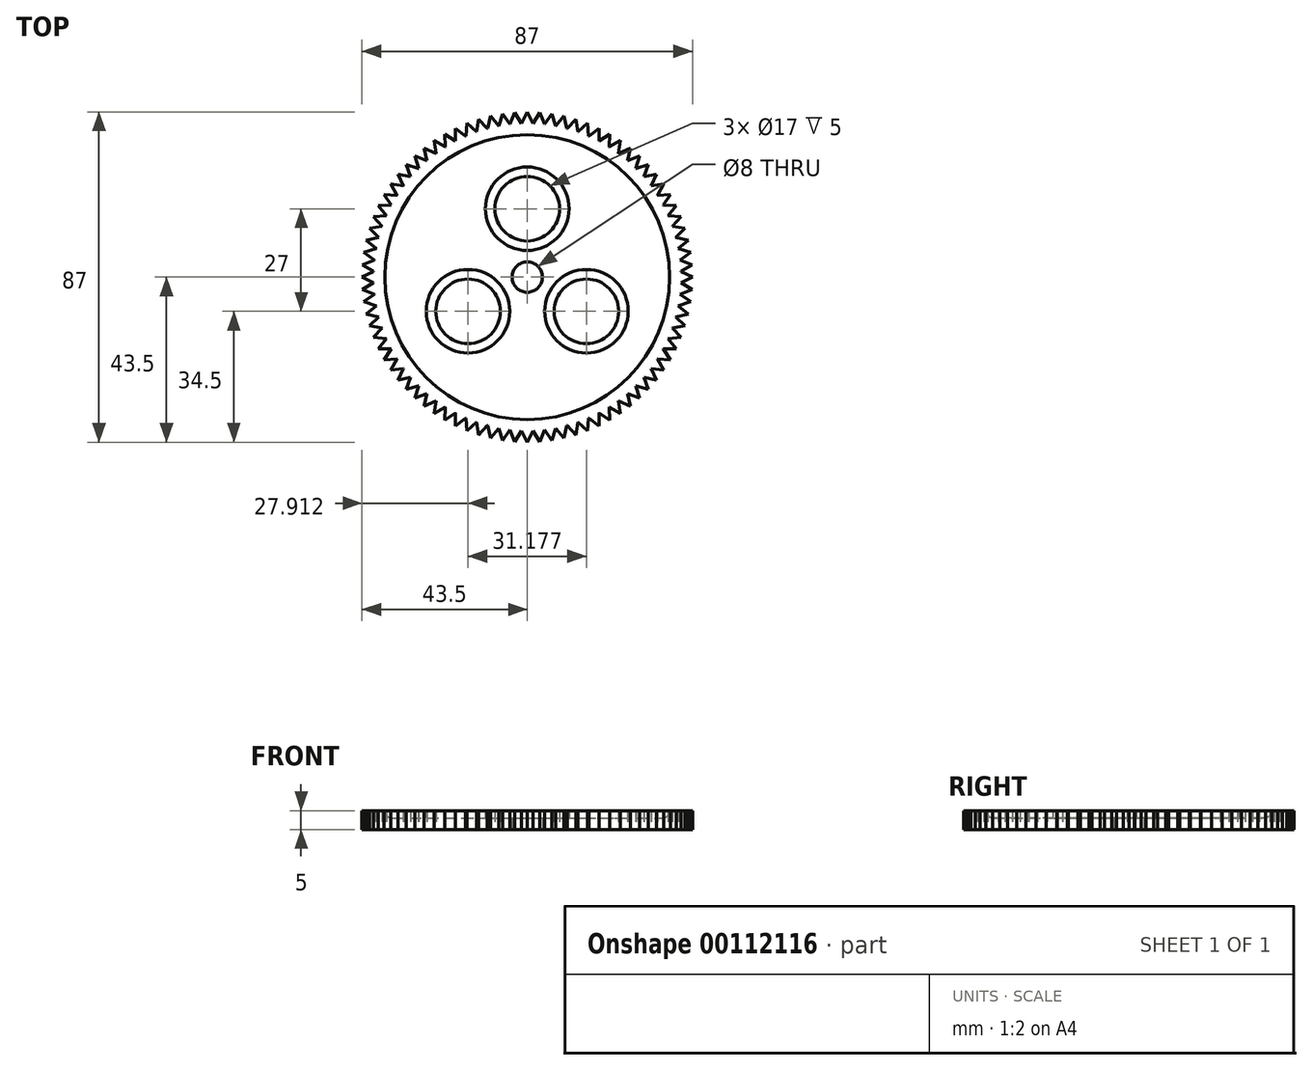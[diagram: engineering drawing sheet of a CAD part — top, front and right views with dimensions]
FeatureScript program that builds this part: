
annotation { "Feature Type Name" : "Feature", "Feature Type Description" : "" }
export const myFeature = defineFeature(function(context is Context, id is Id, definition is map)
    precondition{}
    {
        {
            var Q0;
            Q0=qCreatedBy(makeId("Front.planeOp"),FACE);
            var sketch = newSketch(context, id + "F0", { "sketchPlane" : qUnion([Q0])});
            skLineSegment(sketch, "E0", {"start": v(0, 0) * mm, "end": v(40.5, 0) * mm});
            skLineSegment(sketch, "E1", {"start": v(0, -1.2) * mm, "end": v(0, 3) * mm});
            skLineSegment(sketch, "E2", {"start": v(0, 3) * mm, "end": v(35.5, 3) * mm});
            skLineSegment(sketch, "E3", {"start": v(37.5, 5) * mm, "end": v(37.5, 5) * mm});
            skLineSegment(sketch, "E4", {"start": v(37.5, 5) * mm, "end": v(40.5, 5) * mm});
            skLineSegment(sketch, "E5", {"start": v(40.5, 5) * mm, "end": v(40.5, 0) * mm});
            skPoint(sketch, "E6.visualSharp", {"position": v(37.5, 3) * mm});
            skArc(sketch, "E6.filletArc", {"start": v(35.5, 3) * mm, "mid": v(36.91, 3.59) * mm, "end": v(37.5, 5) * mm});
            skLineSegment(sketch, "E7", {"start": v(4, 3) * mm, "end": v(4, 0) * mm});
            skSolve(sketch);
        }
        {
            var Q0;
            Q0=makeQuery(id+"F0.imprint","IMPRINT",FACE,{"disambiguationData":[TD([[makeQuery(id+"F0.imprint","IMPRINT",EDGE,{"derivedFrom":sQuery(id+"F0.wireOp",EDGE,"E4")}),-1.0]])]});
            var Q1;
            Q1=sQuery(id+"F0.wireOp",EDGE,"E1");
            revolve(context, id + "F1", {"entities" : qUnion([Q0]), "axis" : qUnion([Q1]), "revolveType" : RevolveType.FULL});
        }
        {
            var Q0;
            Q0=qCreatedBy(makeId("Top.planeOp"),FACE);
            var sketch = newSketch(context, id + "F2", { "sketchPlane" : qUnion([Q0])});
            skCircle(sketch, "E8.0.0", {"center": v(0, 0) * mm, "radius": 40.5 * mm});
            skLineSegment(sketch, "E9", {"start": v(0, 40.5) * mm, "end": v(0, 43.5) * mm});
            skLineSegment(sketch, "E10", {"start": v(0, 43.5) * mm, "end": v(-1.5, 40.47) * mm});
            skLineSegment(sketch, "E11", {"start": v(0, 43.5) * mm, "end": v(1.5, 40.47) * mm});
            skLineSegment(sketch, "E12.1.0", {"start": v(-3.25, 43.38) * mm, "end": v(-4.52, 40.25) * mm});
            skLineSegment(sketch, "E12.1.1", {"start": v(-3.25, 43.38) * mm, "end": v(-1.53, 40.47) * mm});
            skLineSegment(sketch, "E12.2.0", {"start": v(-6.48, 43.01) * mm, "end": v(-7.52, 39.8) * mm});
            skLineSegment(sketch, "E12.2.1", {"start": v(-6.48, 43.01) * mm, "end": v(-4.55, 40.24) * mm});
            skLineSegment(sketch, "E12.3.0", {"start": v(-9.68, 42.4) * mm, "end": v(-10.47, 39.12) * mm});
            skLineSegment(sketch, "E12.3.1", {"start": v(-9.68, 42.4) * mm, "end": v(-7.54, 39.8) * mm});
            skLineSegment(sketch, "E12.4.0", {"start": v(-12.82, 41.57) * mm, "end": v(-13.36, 38.23) * mm});
            skLineSegment(sketch, "E12.4.1", {"start": v(-12.82, 41.57) * mm, "end": v(-10.5, 39.12) * mm});
            skLineSegment(sketch, "E12.5.0", {"start": v(-15.9, 40.5) * mm, "end": v(-16.18, 37.13) * mm});
            skLineSegment(sketch, "E12.5.1", {"start": v(-15.9, 40.5) * mm, "end": v(-13.39, 38.22) * mm});
            skLineSegment(sketch, "E12.6.0", {"start": v(-18.87, 39.2) * mm, "end": v(-18.91, 35.81) * mm});
            skLineSegment(sketch, "E12.6.1", {"start": v(-18.87, 39.2) * mm, "end": v(-16.2, 37.12) * mm});
            skLineSegment(sketch, "E12.7.0", {"start": v(-21.75, 37.67) * mm, "end": v(-21.54, 34.3) * mm});
            skLineSegment(sketch, "E12.7.1", {"start": v(-21.75, 37.67) * mm, "end": v(-18.94, 35.8) * mm});
            skLineSegment(sketch, "E12.8.0", {"start": v(-24.5, 35.94) * mm, "end": v(-24.04, 32.6) * mm});
            skLineSegment(sketch, "E12.8.1", {"start": v(-24.5, 35.94) * mm, "end": v(-21.56, 34.28) * mm});
            skLineSegment(sketch, "E12.9.0", {"start": v(-27.12, 34) * mm, "end": v(-26.4, 30.7) * mm});
            skLineSegment(sketch, "E12.9.1", {"start": v(-27.12, 34) * mm, "end": v(-24.06, 32.58) * mm});
            skLineSegment(sketch, "E12.10.0", {"start": v(-29.59, 31.89) * mm, "end": v(-28.63, 28.65) * mm});
            skLineSegment(sketch, "E12.10.1", {"start": v(-29.59, 31.89) * mm, "end": v(-26.43, 30.69) * mm});
            skLineSegment(sketch, "E12.11.0", {"start": v(-31.89, 29.59) * mm, "end": v(-30.69, 26.43) * mm});
            skLineSegment(sketch, "E12.11.1", {"start": v(-31.89, 29.59) * mm, "end": v(-28.65, 28.63) * mm});
            skLineSegment(sketch, "E12.12.0", {"start": v(-34, 27.12) * mm, "end": v(-32.58, 24.06) * mm});
            skLineSegment(sketch, "E12.12.1", {"start": v(-34, 27.12) * mm, "end": v(-30.7, 26.4) * mm});
            skLineSegment(sketch, "E12.13.0", {"start": v(-35.94, 24.5) * mm, "end": v(-34.28, 21.56) * mm});
            skLineSegment(sketch, "E12.13.1", {"start": v(-35.94, 24.5) * mm, "end": v(-32.6, 24.04) * mm});
            skLineSegment(sketch, "E12.14.0", {"start": v(-37.67, 21.75) * mm, "end": v(-35.8, 18.94) * mm});
            skLineSegment(sketch, "E12.14.1", {"start": v(-37.67, 21.75) * mm, "end": v(-34.3, 21.54) * mm});
            skLineSegment(sketch, "E12.15.0", {"start": v(-39.2, 18.87) * mm, "end": v(-37.12, 16.2) * mm});
            skLineSegment(sketch, "E12.15.1", {"start": v(-39.2, 18.87) * mm, "end": v(-35.81, 18.91) * mm});
            skLineSegment(sketch, "E12.16.0", {"start": v(-40.5, 15.9) * mm, "end": v(-38.22, 13.39) * mm});
            skLineSegment(sketch, "E12.16.1", {"start": v(-40.5, 15.9) * mm, "end": v(-37.13, 16.18) * mm});
            skLineSegment(sketch, "E12.17.0", {"start": v(-41.57, 12.82) * mm, "end": v(-39.12, 10.5) * mm});
            skLineSegment(sketch, "E12.17.1", {"start": v(-41.57, 12.82) * mm, "end": v(-38.23, 13.36) * mm});
            skLineSegment(sketch, "E12.18.0", {"start": v(-42.4, 9.68) * mm, "end": v(-39.8, 7.54) * mm});
            skLineSegment(sketch, "E12.18.1", {"start": v(-42.4, 9.68) * mm, "end": v(-39.12, 10.47) * mm});
            skLineSegment(sketch, "E12.19.0", {"start": v(-43.01, 6.48) * mm, "end": v(-40.24, 4.55) * mm});
            skLineSegment(sketch, "E12.19.1", {"start": v(-43.01, 6.48) * mm, "end": v(-39.8, 7.52) * mm});
            skLineSegment(sketch, "E12.20.0", {"start": v(-43.38, 3.25) * mm, "end": v(-40.47, 1.53) * mm});
            skLineSegment(sketch, "E12.20.1", {"start": v(-43.38, 3.25) * mm, "end": v(-40.25, 4.52) * mm});
            skLineSegment(sketch, "E12.21.0", {"start": v(-43.5, 0) * mm, "end": v(-40.47, -1.5) * mm});
            skLineSegment(sketch, "E12.21.1", {"start": v(-43.5, 0) * mm, "end": v(-40.47, 1.5) * mm});
            skLineSegment(sketch, "E12.22.0", {"start": v(-43.38, -3.25) * mm, "end": v(-40.25, -4.52) * mm});
            skLineSegment(sketch, "E12.22.1", {"start": v(-43.38, -3.25) * mm, "end": v(-40.47, -1.53) * mm});
            skLineSegment(sketch, "E12.23.0", {"start": v(-43.01, -6.48) * mm, "end": v(-39.8, -7.52) * mm});
            skLineSegment(sketch, "E12.23.1", {"start": v(-43.01, -6.48) * mm, "end": v(-40.24, -4.55) * mm});
            skLineSegment(sketch, "E12.24.0", {"start": v(-42.4, -9.68) * mm, "end": v(-39.12, -10.47) * mm});
            skLineSegment(sketch, "E12.24.1", {"start": v(-42.4, -9.68) * mm, "end": v(-39.8, -7.54) * mm});
            skLineSegment(sketch, "E12.25.0", {"start": v(-41.57, -12.82) * mm, "end": v(-38.23, -13.36) * mm});
            skLineSegment(sketch, "E12.25.1", {"start": v(-41.57, -12.82) * mm, "end": v(-39.12, -10.5) * mm});
            skLineSegment(sketch, "E12.26.0", {"start": v(-40.5, -15.9) * mm, "end": v(-37.13, -16.18) * mm});
            skLineSegment(sketch, "E12.26.1", {"start": v(-40.5, -15.9) * mm, "end": v(-38.22, -13.39) * mm});
            skLineSegment(sketch, "E12.27.0", {"start": v(-39.2, -18.87) * mm, "end": v(-35.81, -18.91) * mm});
            skLineSegment(sketch, "E12.27.1", {"start": v(-39.2, -18.87) * mm, "end": v(-37.12, -16.2) * mm});
            skLineSegment(sketch, "E12.28.0", {"start": v(-37.67, -21.75) * mm, "end": v(-34.3, -21.54) * mm});
            skLineSegment(sketch, "E12.28.1", {"start": v(-37.67, -21.75) * mm, "end": v(-35.8, -18.94) * mm});
            skLineSegment(sketch, "E12.29.0", {"start": v(-35.94, -24.5) * mm, "end": v(-32.6, -24.04) * mm});
            skLineSegment(sketch, "E12.29.1", {"start": v(-35.94, -24.5) * mm, "end": v(-34.28, -21.56) * mm});
            skLineSegment(sketch, "E12.30.0", {"start": v(-34, -27.12) * mm, "end": v(-30.7, -26.4) * mm});
            skLineSegment(sketch, "E12.30.1", {"start": v(-34, -27.12) * mm, "end": v(-32.58, -24.06) * mm});
            skLineSegment(sketch, "E12.31.0", {"start": v(-31.89, -29.59) * mm, "end": v(-28.65, -28.63) * mm});
            skLineSegment(sketch, "E12.31.1", {"start": v(-31.89, -29.59) * mm, "end": v(-30.69, -26.43) * mm});
            skLineSegment(sketch, "E12.32.0", {"start": v(-29.59, -31.89) * mm, "end": v(-26.43, -30.69) * mm});
            skLineSegment(sketch, "E12.32.1", {"start": v(-29.59, -31.89) * mm, "end": v(-28.63, -28.65) * mm});
            skLineSegment(sketch, "E12.33.0", {"start": v(-27.12, -34) * mm, "end": v(-24.06, -32.58) * mm});
            skLineSegment(sketch, "E12.33.1", {"start": v(-27.12, -34) * mm, "end": v(-26.4, -30.7) * mm});
            skLineSegment(sketch, "E12.34.0", {"start": v(-24.5, -35.94) * mm, "end": v(-21.56, -34.28) * mm});
            skLineSegment(sketch, "E12.34.1", {"start": v(-24.5, -35.94) * mm, "end": v(-24.04, -32.6) * mm});
            skLineSegment(sketch, "E12.35.0", {"start": v(-21.75, -37.67) * mm, "end": v(-18.94, -35.8) * mm});
            skLineSegment(sketch, "E12.35.1", {"start": v(-21.75, -37.67) * mm, "end": v(-21.54, -34.3) * mm});
            skLineSegment(sketch, "E12.36.0", {"start": v(-18.87, -39.2) * mm, "end": v(-16.2, -37.12) * mm});
            skLineSegment(sketch, "E12.36.1", {"start": v(-18.87, -39.2) * mm, "end": v(-18.91, -35.81) * mm});
            skLineSegment(sketch, "E12.37.0", {"start": v(-15.9, -40.5) * mm, "end": v(-13.39, -38.22) * mm});
            skLineSegment(sketch, "E12.37.1", {"start": v(-15.9, -40.5) * mm, "end": v(-16.18, -37.13) * mm});
            skLineSegment(sketch, "E12.38.0", {"start": v(-12.82, -41.57) * mm, "end": v(-10.5, -39.12) * mm});
            skLineSegment(sketch, "E12.38.1", {"start": v(-12.82, -41.57) * mm, "end": v(-13.36, -38.23) * mm});
            skLineSegment(sketch, "E12.39.0", {"start": v(-9.68, -42.4) * mm, "end": v(-7.54, -39.8) * mm});
            skLineSegment(sketch, "E12.39.1", {"start": v(-9.68, -42.4) * mm, "end": v(-10.47, -39.12) * mm});
            skLineSegment(sketch, "E12.40.0", {"start": v(-6.48, -43.01) * mm, "end": v(-4.55, -40.24) * mm});
            skLineSegment(sketch, "E12.40.1", {"start": v(-6.48, -43.01) * mm, "end": v(-7.52, -39.8) * mm});
            skLineSegment(sketch, "E12.41.0", {"start": v(-3.25, -43.38) * mm, "end": v(-1.53, -40.47) * mm});
            skLineSegment(sketch, "E12.41.1", {"start": v(-3.25, -43.38) * mm, "end": v(-4.52, -40.25) * mm});
            skLineSegment(sketch, "E12.42.0", {"start": v(0, -43.5) * mm, "end": v(1.5, -40.47) * mm});
            skLineSegment(sketch, "E12.42.1", {"start": v(0, -43.5) * mm, "end": v(-1.5, -40.47) * mm});
            skLineSegment(sketch, "E12.43.0", {"start": v(3.25, -43.38) * mm, "end": v(4.52, -40.25) * mm});
            skLineSegment(sketch, "E12.43.1", {"start": v(3.25, -43.38) * mm, "end": v(1.53, -40.47) * mm});
            skLineSegment(sketch, "E12.44.0", {"start": v(6.48, -43.01) * mm, "end": v(7.52, -39.8) * mm});
            skLineSegment(sketch, "E12.44.1", {"start": v(6.48, -43.01) * mm, "end": v(4.55, -40.24) * mm});
            skLineSegment(sketch, "E12.45.0", {"start": v(9.68, -42.4) * mm, "end": v(10.47, -39.12) * mm});
            skLineSegment(sketch, "E12.45.1", {"start": v(9.68, -42.4) * mm, "end": v(7.54, -39.8) * mm});
            skLineSegment(sketch, "E13.2.46.0", {"start": v(12.82, -41.57) * mm, "end": v(13.36, -38.23) * mm});
            skLineSegment(sketch, "E13.3.46.0", {"start": v(12.82, -41.57) * mm, "end": v(10.5, -39.12) * mm});
            skLineSegment(sketch, "E13.2.47.0", {"start": v(15.9, -40.5) * mm, "end": v(16.18, -37.13) * mm});
            skLineSegment(sketch, "E13.3.47.0", {"start": v(15.9, -40.5) * mm, "end": v(13.39, -38.22) * mm});
            skLineSegment(sketch, "E13.2.48.0", {"start": v(18.87, -39.2) * mm, "end": v(18.91, -35.81) * mm});
            skLineSegment(sketch, "E13.3.48.0", {"start": v(18.87, -39.2) * mm, "end": v(16.2, -37.12) * mm});
            skLineSegment(sketch, "E13.2.49.0", {"start": v(21.75, -37.67) * mm, "end": v(21.54, -34.3) * mm});
            skLineSegment(sketch, "E13.3.49.0", {"start": v(21.75, -37.67) * mm, "end": v(18.94, -35.8) * mm});
            skLineSegment(sketch, "E13.2.50.0", {"start": v(24.5, -35.94) * mm, "end": v(24.04, -32.6) * mm});
            skLineSegment(sketch, "E13.3.50.0", {"start": v(24.5, -35.94) * mm, "end": v(21.56, -34.28) * mm});
            skLineSegment(sketch, "E13.2.51.0", {"start": v(27.12, -34) * mm, "end": v(26.4, -30.7) * mm});
            skLineSegment(sketch, "E13.3.51.0", {"start": v(27.12, -34) * mm, "end": v(24.06, -32.58) * mm});
            skLineSegment(sketch, "E13.2.52.0", {"start": v(29.59, -31.89) * mm, "end": v(28.63, -28.65) * mm});
            skLineSegment(sketch, "E13.3.52.0", {"start": v(29.59, -31.89) * mm, "end": v(26.43, -30.69) * mm});
            skLineSegment(sketch, "E13.2.53.0", {"start": v(31.89, -29.59) * mm, "end": v(30.69, -26.43) * mm});
            skLineSegment(sketch, "E13.3.53.0", {"start": v(31.89, -29.59) * mm, "end": v(28.65, -28.63) * mm});
            skLineSegment(sketch, "E13.2.54.0", {"start": v(34, -27.12) * mm, "end": v(32.58, -24.06) * mm});
            skLineSegment(sketch, "E13.3.54.0", {"start": v(34, -27.12) * mm, "end": v(30.7, -26.4) * mm});
            skLineSegment(sketch, "E13.2.55.0", {"start": v(35.94, -24.5) * mm, "end": v(34.28, -21.56) * mm});
            skLineSegment(sketch, "E13.3.55.0", {"start": v(35.94, -24.5) * mm, "end": v(32.6, -24.04) * mm});
            skLineSegment(sketch, "E13.2.56.0", {"start": v(37.67, -21.75) * mm, "end": v(35.8, -18.94) * mm});
            skLineSegment(sketch, "E13.3.56.0", {"start": v(37.67, -21.75) * mm, "end": v(34.3, -21.54) * mm});
            skLineSegment(sketch, "E13.2.57.0", {"start": v(39.2, -18.87) * mm, "end": v(37.12, -16.2) * mm});
            skLineSegment(sketch, "E13.3.57.0", {"start": v(39.2, -18.87) * mm, "end": v(35.81, -18.91) * mm});
            skLineSegment(sketch, "E13.2.58.0", {"start": v(40.5, -15.9) * mm, "end": v(38.22, -13.39) * mm});
            skLineSegment(sketch, "E13.3.58.0", {"start": v(40.5, -15.9) * mm, "end": v(37.13, -16.18) * mm});
            skLineSegment(sketch, "E13.2.59.0", {"start": v(41.57, -12.82) * mm, "end": v(39.12, -10.5) * mm});
            skLineSegment(sketch, "E13.3.59.0", {"start": v(41.57, -12.82) * mm, "end": v(38.23, -13.36) * mm});
            skLineSegment(sketch, "E13.2.60.0", {"start": v(42.4, -9.68) * mm, "end": v(39.8, -7.54) * mm});
            skLineSegment(sketch, "E13.3.60.0", {"start": v(42.4, -9.68) * mm, "end": v(39.12, -10.47) * mm});
            skLineSegment(sketch, "E13.2.61.0", {"start": v(43.01, -6.48) * mm, "end": v(40.24, -4.55) * mm});
            skLineSegment(sketch, "E13.3.61.0", {"start": v(43.01, -6.48) * mm, "end": v(39.8, -7.52) * mm});
            skLineSegment(sketch, "E13.2.62.0", {"start": v(43.38, -3.25) * mm, "end": v(40.47, -1.53) * mm});
            skLineSegment(sketch, "E13.3.62.0", {"start": v(43.38, -3.25) * mm, "end": v(40.25, -4.52) * mm});
            skLineSegment(sketch, "E13.2.63.0", {"start": v(43.5, 0) * mm, "end": v(40.47, 1.5) * mm});
            skLineSegment(sketch, "E13.3.63.0", {"start": v(43.5, 0) * mm, "end": v(40.47, -1.5) * mm});
            skLineSegment(sketch, "E13.2.64.0", {"start": v(43.38, 3.25) * mm, "end": v(40.25, 4.52) * mm});
            skLineSegment(sketch, "E13.3.64.0", {"start": v(43.38, 3.25) * mm, "end": v(40.47, 1.53) * mm});
            skLineSegment(sketch, "E13.2.65.0", {"start": v(43.01, 6.48) * mm, "end": v(39.8, 7.52) * mm});
            skLineSegment(sketch, "E13.3.65.0", {"start": v(43.01, 6.48) * mm, "end": v(40.24, 4.55) * mm});
            skLineSegment(sketch, "E13.2.66.0", {"start": v(42.4, 9.68) * mm, "end": v(39.12, 10.47) * mm});
            skLineSegment(sketch, "E13.3.66.0", {"start": v(42.4, 9.68) * mm, "end": v(39.8, 7.54) * mm});
            skLineSegment(sketch, "E13.2.67.0", {"start": v(41.57, 12.82) * mm, "end": v(38.23, 13.36) * mm});
            skLineSegment(sketch, "E13.3.67.0", {"start": v(41.57, 12.82) * mm, "end": v(39.12, 10.5) * mm});
            skLineSegment(sketch, "E13.2.68.0", {"start": v(40.5, 15.9) * mm, "end": v(37.13, 16.18) * mm});
            skLineSegment(sketch, "E13.3.68.0", {"start": v(40.5, 15.9) * mm, "end": v(38.22, 13.39) * mm});
            skLineSegment(sketch, "E13.2.69.0", {"start": v(39.2, 18.87) * mm, "end": v(35.81, 18.91) * mm});
            skLineSegment(sketch, "E13.3.69.0", {"start": v(39.2, 18.87) * mm, "end": v(37.12, 16.2) * mm});
            skLineSegment(sketch, "E13.2.70.0", {"start": v(37.67, 21.75) * mm, "end": v(34.3, 21.54) * mm});
            skLineSegment(sketch, "E13.3.70.0", {"start": v(37.67, 21.75) * mm, "end": v(35.8, 18.94) * mm});
            skLineSegment(sketch, "E13.2.71.0", {"start": v(35.94, 24.5) * mm, "end": v(32.6, 24.04) * mm});
            skLineSegment(sketch, "E13.3.71.0", {"start": v(35.94, 24.5) * mm, "end": v(34.28, 21.56) * mm});
            skLineSegment(sketch, "E13.2.72.0", {"start": v(34, 27.12) * mm, "end": v(30.7, 26.4) * mm});
            skLineSegment(sketch, "E13.3.72.0", {"start": v(34, 27.12) * mm, "end": v(32.58, 24.06) * mm});
            skLineSegment(sketch, "E13.2.73.0", {"start": v(31.89, 29.59) * mm, "end": v(28.65, 28.63) * mm});
            skLineSegment(sketch, "E13.3.73.0", {"start": v(31.89, 29.59) * mm, "end": v(30.69, 26.43) * mm});
            skLineSegment(sketch, "E13.2.74.0", {"start": v(29.59, 31.89) * mm, "end": v(26.43, 30.69) * mm});
            skLineSegment(sketch, "E13.3.74.0", {"start": v(29.59, 31.89) * mm, "end": v(28.63, 28.65) * mm});
            skLineSegment(sketch, "E13.2.75.0", {"start": v(27.12, 34) * mm, "end": v(24.06, 32.58) * mm});
            skLineSegment(sketch, "E13.3.75.0", {"start": v(27.12, 34) * mm, "end": v(26.4, 30.7) * mm});
            skLineSegment(sketch, "E13.2.76.0", {"start": v(24.5, 35.94) * mm, "end": v(21.56, 34.28) * mm});
            skLineSegment(sketch, "E13.3.76.0", {"start": v(24.5, 35.94) * mm, "end": v(24.04, 32.6) * mm});
            skLineSegment(sketch, "E13.2.77.0", {"start": v(21.75, 37.67) * mm, "end": v(18.94, 35.8) * mm});
            skLineSegment(sketch, "E13.3.77.0", {"start": v(21.75, 37.67) * mm, "end": v(21.54, 34.3) * mm});
            skLineSegment(sketch, "E13.2.78.0", {"start": v(18.87, 39.2) * mm, "end": v(16.2, 37.12) * mm});
            skLineSegment(sketch, "E13.3.78.0", {"start": v(18.87, 39.2) * mm, "end": v(18.91, 35.81) * mm});
            skLineSegment(sketch, "E13.2.79.0", {"start": v(15.9, 40.5) * mm, "end": v(13.39, 38.22) * mm});
            skLineSegment(sketch, "E13.3.79.0", {"start": v(15.9, 40.5) * mm, "end": v(16.18, 37.13) * mm});
            skLineSegment(sketch, "E14.2.80.0", {"start": v(12.82, 41.57) * mm, "end": v(10.5, 39.12) * mm});
            skLineSegment(sketch, "E14.3.80.0", {"start": v(12.82, 41.57) * mm, "end": v(13.36, 38.23) * mm});
            skLineSegment(sketch, "E14.2.81.0", {"start": v(9.68, 42.4) * mm, "end": v(7.54, 39.8) * mm});
            skLineSegment(sketch, "E14.3.81.0", {"start": v(9.68, 42.4) * mm, "end": v(10.47, 39.12) * mm});
            skLineSegment(sketch, "E15.2.82.0", {"start": v(6.48, 43.01) * mm, "end": v(4.55, 40.24) * mm});
            skLineSegment(sketch, "E15.3.82.0", {"start": v(6.48, 43.01) * mm, "end": v(7.52, 39.8) * mm});
            skLineSegment(sketch, "E15.2.83.0", {"start": v(3.25, 43.38) * mm, "end": v(1.53, 40.47) * mm});
            skLineSegment(sketch, "E15.3.83.0", {"start": v(3.25, 43.38) * mm, "end": v(4.52, 40.25) * mm});
            skSolve(sketch);
        }
        {
            var Q0;
            {var subQ0=sQuery(id+"F2.wireOp",EDGE,"E9");Q0=makeQuery(id+"F2.imprint","IMPRINT",FACE,{"disambiguationData":[TD([[makeQuery(id+"F2.imprint","IMPRINT",EDGE,{"derivedFrom":subQ0}),1.0]])]});}
            var Q1;
            {var subQ0=sQuery(id+"F2.wireOp",EDGE,"E9");Q1=makeQuery(id+"F2.imprint","IMPRINT",FACE,{"disambiguationData":[TD([[makeQuery(id+"F2.imprint","IMPRINT",EDGE,{"derivedFrom":subQ0}),-1.0]])]});}
            var Q2;
            {var subQ0=sQuery(id+"F2.wireOp",EDGE,"E12.45.0");Q2=makeQuery(id+"F2.imprint","IMPRINT",FACE,{"disambiguationData":[TD([[makeQuery(id+"F2.imprint","IMPRINT",EDGE,{"derivedFrom":subQ0}),1.0]])]});}
            var Q3;
            {var subQ0=sQuery(id+"F2.wireOp",EDGE,"E12.44.0");Q3=makeQuery(id+"F2.imprint","IMPRINT",FACE,{"disambiguationData":[TD([[makeQuery(id+"F2.imprint","IMPRINT",EDGE,{"derivedFrom":subQ0}),1.0]])]});}
            var Q4;
            {var subQ0=sQuery(id+"F2.wireOp",EDGE,"E12.43.0");Q4=makeQuery(id+"F2.imprint","IMPRINT",FACE,{"disambiguationData":[TD([[makeQuery(id+"F2.imprint","IMPRINT",EDGE,{"derivedFrom":subQ0}),1.0]])]});}
            var Q5;
            {var subQ0=sQuery(id+"F2.wireOp",EDGE,"E12.42.0");Q5=makeQuery(id+"F2.imprint","IMPRINT",FACE,{"disambiguationData":[TD([[makeQuery(id+"F2.imprint","IMPRINT",EDGE,{"derivedFrom":subQ0}),1.0]])]});}
            var Q6;
            {var subQ0=sQuery(id+"F2.wireOp",EDGE,"E12.41.0");Q6=makeQuery(id+"F2.imprint","IMPRINT",FACE,{"disambiguationData":[TD([[makeQuery(id+"F2.imprint","IMPRINT",EDGE,{"derivedFrom":subQ0}),1.0]])]});}
            var Q7;
            {var subQ0=sQuery(id+"F2.wireOp",EDGE,"E12.40.0");Q7=makeQuery(id+"F2.imprint","IMPRINT",FACE,{"disambiguationData":[TD([[makeQuery(id+"F2.imprint","IMPRINT",EDGE,{"derivedFrom":subQ0}),1.0]])]});}
            var Q8;
            {var subQ0=sQuery(id+"F2.wireOp",EDGE,"E12.39.0");Q8=makeQuery(id+"F2.imprint","IMPRINT",FACE,{"disambiguationData":[TD([[makeQuery(id+"F2.imprint","IMPRINT",EDGE,{"derivedFrom":subQ0}),1.0]])]});}
            var Q9;
            {var subQ0=sQuery(id+"F2.wireOp",EDGE,"E12.38.0");Q9=makeQuery(id+"F2.imprint","IMPRINT",FACE,{"disambiguationData":[TD([[makeQuery(id+"F2.imprint","IMPRINT",EDGE,{"derivedFrom":subQ0}),1.0]])]});}
            var Q10;
            {var subQ0=sQuery(id+"F2.wireOp",EDGE,"E12.37.0");Q10=makeQuery(id+"F2.imprint","IMPRINT",FACE,{"disambiguationData":[TD([[makeQuery(id+"F2.imprint","IMPRINT",EDGE,{"derivedFrom":subQ0}),1.0]])]});}
            var Q11;
            {var subQ0=sQuery(id+"F2.wireOp",EDGE,"E12.36.0");Q11=makeQuery(id+"F2.imprint","IMPRINT",FACE,{"disambiguationData":[TD([[makeQuery(id+"F2.imprint","IMPRINT",EDGE,{"derivedFrom":subQ0}),1.0]])]});}
            var Q12;
            {var subQ0=sQuery(id+"F2.wireOp",EDGE,"E12.35.0");Q12=makeQuery(id+"F2.imprint","IMPRINT",FACE,{"disambiguationData":[TD([[makeQuery(id+"F2.imprint","IMPRINT",EDGE,{"derivedFrom":subQ0}),1.0]])]});}
            var Q13;
            {var subQ0=sQuery(id+"F2.wireOp",EDGE,"E12.34.0");Q13=makeQuery(id+"F2.imprint","IMPRINT",FACE,{"disambiguationData":[TD([[makeQuery(id+"F2.imprint","IMPRINT",EDGE,{"derivedFrom":subQ0}),1.0]])]});}
            var Q14;
            {var subQ0=sQuery(id+"F2.wireOp",EDGE,"E12.33.0");Q14=makeQuery(id+"F2.imprint","IMPRINT",FACE,{"disambiguationData":[TD([[makeQuery(id+"F2.imprint","IMPRINT",EDGE,{"derivedFrom":subQ0}),1.0]])]});}
            var Q15;
            {var subQ0=sQuery(id+"F2.wireOp",EDGE,"E12.32.0");Q15=makeQuery(id+"F2.imprint","IMPRINT",FACE,{"disambiguationData":[TD([[makeQuery(id+"F2.imprint","IMPRINT",EDGE,{"derivedFrom":subQ0}),1.0]])]});}
            var Q16;
            {var subQ0=sQuery(id+"F2.wireOp",EDGE,"E12.31.0");Q16=makeQuery(id+"F2.imprint","IMPRINT",FACE,{"disambiguationData":[TD([[makeQuery(id+"F2.imprint","IMPRINT",EDGE,{"derivedFrom":subQ0}),1.0]])]});}
            var Q17;
            {var subQ0=sQuery(id+"F2.wireOp",EDGE,"E12.1.0");Q17=makeQuery(id+"F2.imprint","IMPRINT",FACE,{"disambiguationData":[TD([[makeQuery(id+"F2.imprint","IMPRINT",EDGE,{"derivedFrom":subQ0}),1.0]])]});}
            var Q18;
            {var subQ0=sQuery(id+"F2.wireOp",EDGE,"E12.2.0");Q18=makeQuery(id+"F2.imprint","IMPRINT",FACE,{"disambiguationData":[TD([[makeQuery(id+"F2.imprint","IMPRINT",EDGE,{"derivedFrom":subQ0}),1.0]])]});}
            var Q19;
            {var subQ0=sQuery(id+"F2.wireOp",EDGE,"E12.3.0");Q19=makeQuery(id+"F2.imprint","IMPRINT",FACE,{"disambiguationData":[TD([[makeQuery(id+"F2.imprint","IMPRINT",EDGE,{"derivedFrom":subQ0}),1.0]])]});}
            var Q20;
            {var subQ0=sQuery(id+"F2.wireOp",EDGE,"E12.4.0");Q20=makeQuery(id+"F2.imprint","IMPRINT",FACE,{"disambiguationData":[TD([[makeQuery(id+"F2.imprint","IMPRINT",EDGE,{"derivedFrom":subQ0}),1.0]])]});}
            var Q21;
            {var subQ0=sQuery(id+"F2.wireOp",EDGE,"E12.5.0");Q21=makeQuery(id+"F2.imprint","IMPRINT",FACE,{"disambiguationData":[TD([[makeQuery(id+"F2.imprint","IMPRINT",EDGE,{"derivedFrom":subQ0}),1.0]])]});}
            var Q22;
            {var subQ0=sQuery(id+"F2.wireOp",EDGE,"E12.6.0");Q22=makeQuery(id+"F2.imprint","IMPRINT",FACE,{"disambiguationData":[TD([[makeQuery(id+"F2.imprint","IMPRINT",EDGE,{"derivedFrom":subQ0}),1.0]])]});}
            var Q23;
            {var subQ0=sQuery(id+"F2.wireOp",EDGE,"E12.7.0");Q23=makeQuery(id+"F2.imprint","IMPRINT",FACE,{"disambiguationData":[TD([[makeQuery(id+"F2.imprint","IMPRINT",EDGE,{"derivedFrom":subQ0}),1.0]])]});}
            var Q24;
            {var subQ0=sQuery(id+"F2.wireOp",EDGE,"E12.8.0");Q24=makeQuery(id+"F2.imprint","IMPRINT",FACE,{"disambiguationData":[TD([[makeQuery(id+"F2.imprint","IMPRINT",EDGE,{"derivedFrom":subQ0}),1.0]])]});}
            var Q25;
            {var subQ0=sQuery(id+"F2.wireOp",EDGE,"E12.9.0");Q25=makeQuery(id+"F2.imprint","IMPRINT",FACE,{"disambiguationData":[TD([[makeQuery(id+"F2.imprint","IMPRINT",EDGE,{"derivedFrom":subQ0}),1.0]])]});}
            var Q26;
            {var subQ0=sQuery(id+"F2.wireOp",EDGE,"E12.10.0");Q26=makeQuery(id+"F2.imprint","IMPRINT",FACE,{"disambiguationData":[TD([[makeQuery(id+"F2.imprint","IMPRINT",EDGE,{"derivedFrom":subQ0}),1.0]])]});}
            var Q27;
            {var subQ0=sQuery(id+"F2.wireOp",EDGE,"E12.11.0");Q27=makeQuery(id+"F2.imprint","IMPRINT",FACE,{"disambiguationData":[TD([[makeQuery(id+"F2.imprint","IMPRINT",EDGE,{"derivedFrom":subQ0}),1.0]])]});}
            var Q28;
            {var subQ0=sQuery(id+"F2.wireOp",EDGE,"E12.12.0");Q28=makeQuery(id+"F2.imprint","IMPRINT",FACE,{"disambiguationData":[TD([[makeQuery(id+"F2.imprint","IMPRINT",EDGE,{"derivedFrom":subQ0}),1.0]])]});}
            var Q29;
            {var subQ0=sQuery(id+"F2.wireOp",EDGE,"E12.13.0");Q29=makeQuery(id+"F2.imprint","IMPRINT",FACE,{"disambiguationData":[TD([[makeQuery(id+"F2.imprint","IMPRINT",EDGE,{"derivedFrom":subQ0}),1.0]])]});}
            var Q30;
            {var subQ0=sQuery(id+"F2.wireOp",EDGE,"E12.14.0");Q30=makeQuery(id+"F2.imprint","IMPRINT",FACE,{"disambiguationData":[TD([[makeQuery(id+"F2.imprint","IMPRINT",EDGE,{"derivedFrom":subQ0}),1.0]])]});}
            var Q31;
            {var subQ0=sQuery(id+"F2.wireOp",EDGE,"E12.20.0");Q31=makeQuery(id+"F2.imprint","IMPRINT",FACE,{"disambiguationData":[TD([[makeQuery(id+"F2.imprint","IMPRINT",EDGE,{"derivedFrom":subQ0}),1.0]])]});}
            var Q32;
            {var subQ0=sQuery(id+"F2.wireOp",EDGE,"E12.19.0");Q32=makeQuery(id+"F2.imprint","IMPRINT",FACE,{"disambiguationData":[TD([[makeQuery(id+"F2.imprint","IMPRINT",EDGE,{"derivedFrom":subQ0}),1.0]])]});}
            var Q33;
            {var subQ0=sQuery(id+"F2.wireOp",EDGE,"E12.18.0");Q33=makeQuery(id+"F2.imprint","IMPRINT",FACE,{"disambiguationData":[TD([[makeQuery(id+"F2.imprint","IMPRINT",EDGE,{"derivedFrom":subQ0}),1.0]])]});}
            var Q34;
            {var subQ0=sQuery(id+"F2.wireOp",EDGE,"E12.17.0");Q34=makeQuery(id+"F2.imprint","IMPRINT",FACE,{"disambiguationData":[TD([[makeQuery(id+"F2.imprint","IMPRINT",EDGE,{"derivedFrom":subQ0}),1.0]])]});}
            var Q35;
            {var subQ0=sQuery(id+"F2.wireOp",EDGE,"E12.16.0");Q35=makeQuery(id+"F2.imprint","IMPRINT",FACE,{"disambiguationData":[TD([[makeQuery(id+"F2.imprint","IMPRINT",EDGE,{"derivedFrom":subQ0}),1.0]])]});}
            var Q36;
            {var subQ0=sQuery(id+"F2.wireOp",EDGE,"E12.15.0");Q36=makeQuery(id+"F2.imprint","IMPRINT",FACE,{"disambiguationData":[TD([[makeQuery(id+"F2.imprint","IMPRINT",EDGE,{"derivedFrom":subQ0}),1.0]])]});}
            var Q37;
            {var subQ0=sQuery(id+"F2.wireOp",EDGE,"E12.21.0");Q37=makeQuery(id+"F2.imprint","IMPRINT",FACE,{"disambiguationData":[TD([[makeQuery(id+"F2.imprint","IMPRINT",EDGE,{"derivedFrom":subQ0}),1.0]])]});}
            var Q38;
            {var subQ0=sQuery(id+"F2.wireOp",EDGE,"E12.22.0");Q38=makeQuery(id+"F2.imprint","IMPRINT",FACE,{"disambiguationData":[TD([[makeQuery(id+"F2.imprint","IMPRINT",EDGE,{"derivedFrom":subQ0}),1.0]])]});}
            var Q39;
            {var subQ0=sQuery(id+"F2.wireOp",EDGE,"E12.23.0");Q39=makeQuery(id+"F2.imprint","IMPRINT",FACE,{"disambiguationData":[TD([[makeQuery(id+"F2.imprint","IMPRINT",EDGE,{"derivedFrom":subQ0}),1.0]])]});}
            var Q40;
            {var subQ0=sQuery(id+"F2.wireOp",EDGE,"E12.24.0");Q40=makeQuery(id+"F2.imprint","IMPRINT",FACE,{"disambiguationData":[TD([[makeQuery(id+"F2.imprint","IMPRINT",EDGE,{"derivedFrom":subQ0}),1.0]])]});}
            var Q41;
            {var subQ0=sQuery(id+"F2.wireOp",EDGE,"E12.25.0");Q41=makeQuery(id+"F2.imprint","IMPRINT",FACE,{"disambiguationData":[TD([[makeQuery(id+"F2.imprint","IMPRINT",EDGE,{"derivedFrom":subQ0}),1.0]])]});}
            var Q42;
            {var subQ0=sQuery(id+"F2.wireOp",EDGE,"E12.26.0");Q42=makeQuery(id+"F2.imprint","IMPRINT",FACE,{"disambiguationData":[TD([[makeQuery(id+"F2.imprint","IMPRINT",EDGE,{"derivedFrom":subQ0}),1.0]])]});}
            var Q43;
            {var subQ0=sQuery(id+"F2.wireOp",EDGE,"E12.27.0");Q43=makeQuery(id+"F2.imprint","IMPRINT",FACE,{"disambiguationData":[TD([[makeQuery(id+"F2.imprint","IMPRINT",EDGE,{"derivedFrom":subQ0}),1.0]])]});}
            var Q44;
            {var subQ0=sQuery(id+"F2.wireOp",EDGE,"E12.28.0");Q44=makeQuery(id+"F2.imprint","IMPRINT",FACE,{"disambiguationData":[TD([[makeQuery(id+"F2.imprint","IMPRINT",EDGE,{"derivedFrom":subQ0}),1.0]])]});}
            var Q45;
            {var subQ0=sQuery(id+"F2.wireOp",EDGE,"E12.29.0");Q45=makeQuery(id+"F2.imprint","IMPRINT",FACE,{"disambiguationData":[TD([[makeQuery(id+"F2.imprint","IMPRINT",EDGE,{"derivedFrom":subQ0}),1.0]])]});}
            var Q46;
            {var subQ0=sQuery(id+"F2.wireOp",EDGE,"E12.30.0");Q46=makeQuery(id+"F2.imprint","IMPRINT",FACE,{"disambiguationData":[TD([[makeQuery(id+"F2.imprint","IMPRINT",EDGE,{"derivedFrom":subQ0}),1.0]])]});}
            var Q47;
            {var subQ0=sQuery(id+"F2.wireOp",EDGE,"E15.2.83.0");Q47=makeQuery(id+"F2.imprint","IMPRINT",FACE,{"disambiguationData":[TD([[makeQuery(id+"F2.imprint","IMPRINT",EDGE,{"derivedFrom":subQ0}),1.0]])]});}
            var Q48;
            {var subQ0=sQuery(id+"F2.wireOp",EDGE,"E15.2.82.0");Q48=makeQuery(id+"F2.imprint","IMPRINT",FACE,{"disambiguationData":[TD([[makeQuery(id+"F2.imprint","IMPRINT",EDGE,{"derivedFrom":subQ0}),1.0]])]});}
            var Q49;
            {var subQ0=sQuery(id+"F2.wireOp",EDGE,"E14.2.81.0");Q49=makeQuery(id+"F2.imprint","IMPRINT",FACE,{"disambiguationData":[TD([[makeQuery(id+"F2.imprint","IMPRINT",EDGE,{"derivedFrom":subQ0}),1.0]])]});}
            var Q50;
            {var subQ0=sQuery(id+"F2.wireOp",EDGE,"E14.2.80.0");Q50=makeQuery(id+"F2.imprint","IMPRINT",FACE,{"disambiguationData":[TD([[makeQuery(id+"F2.imprint","IMPRINT",EDGE,{"derivedFrom":subQ0}),1.0]])]});}
            var Q51;
            {var subQ0=sQuery(id+"F2.wireOp",EDGE,"E13.2.79.0");Q51=makeQuery(id+"F2.imprint","IMPRINT",FACE,{"disambiguationData":[TD([[makeQuery(id+"F2.imprint","IMPRINT",EDGE,{"derivedFrom":subQ0}),1.0]])]});}
            var Q52;
            {var subQ0=sQuery(id+"F2.wireOp",EDGE,"E13.2.78.0");Q52=makeQuery(id+"F2.imprint","IMPRINT",FACE,{"disambiguationData":[TD([[makeQuery(id+"F2.imprint","IMPRINT",EDGE,{"derivedFrom":subQ0}),1.0]])]});}
            var Q53;
            {var subQ0=sQuery(id+"F2.wireOp",EDGE,"E13.2.77.0");Q53=makeQuery(id+"F2.imprint","IMPRINT",FACE,{"disambiguationData":[TD([[makeQuery(id+"F2.imprint","IMPRINT",EDGE,{"derivedFrom":subQ0}),1.0]])]});}
            var Q54;
            {var subQ0=sQuery(id+"F2.wireOp",EDGE,"E13.2.76.0");Q54=makeQuery(id+"F2.imprint","IMPRINT",FACE,{"disambiguationData":[TD([[makeQuery(id+"F2.imprint","IMPRINT",EDGE,{"derivedFrom":subQ0}),1.0]])]});}
            var Q55;
            {var subQ0=sQuery(id+"F2.wireOp",EDGE,"E13.2.75.0");Q55=makeQuery(id+"F2.imprint","IMPRINT",FACE,{"disambiguationData":[TD([[makeQuery(id+"F2.imprint","IMPRINT",EDGE,{"derivedFrom":subQ0}),1.0]])]});}
            var Q56;
            {var subQ0=sQuery(id+"F2.wireOp",EDGE,"E13.2.74.0");Q56=makeQuery(id+"F2.imprint","IMPRINT",FACE,{"disambiguationData":[TD([[makeQuery(id+"F2.imprint","IMPRINT",EDGE,{"derivedFrom":subQ0}),1.0]])]});}
            var Q57;
            {var subQ0=sQuery(id+"F2.wireOp",EDGE,"E13.2.73.0");Q57=makeQuery(id+"F2.imprint","IMPRINT",FACE,{"disambiguationData":[TD([[makeQuery(id+"F2.imprint","IMPRINT",EDGE,{"derivedFrom":subQ0}),1.0]])]});}
            var Q58;
            {var subQ0=sQuery(id+"F2.wireOp",EDGE,"E13.2.72.0");Q58=makeQuery(id+"F2.imprint","IMPRINT",FACE,{"disambiguationData":[TD([[makeQuery(id+"F2.imprint","IMPRINT",EDGE,{"derivedFrom":subQ0}),1.0]])]});}
            var Q59;
            {var subQ0=sQuery(id+"F2.wireOp",EDGE,"E13.2.71.0");Q59=makeQuery(id+"F2.imprint","IMPRINT",FACE,{"disambiguationData":[TD([[makeQuery(id+"F2.imprint","IMPRINT",EDGE,{"derivedFrom":subQ0}),1.0]])]});}
            var Q60;
            {var subQ0=sQuery(id+"F2.wireOp",EDGE,"E13.2.70.0");Q60=makeQuery(id+"F2.imprint","IMPRINT",FACE,{"disambiguationData":[TD([[makeQuery(id+"F2.imprint","IMPRINT",EDGE,{"derivedFrom":subQ0}),1.0]])]});}
            var Q61;
            {var subQ0=sQuery(id+"F2.wireOp",EDGE,"E13.2.69.0");Q61=makeQuery(id+"F2.imprint","IMPRINT",FACE,{"disambiguationData":[TD([[makeQuery(id+"F2.imprint","IMPRINT",EDGE,{"derivedFrom":subQ0}),1.0]])]});}
            var Q62;
            {var subQ0=sQuery(id+"F2.wireOp",EDGE,"E13.2.68.0");Q62=makeQuery(id+"F2.imprint","IMPRINT",FACE,{"disambiguationData":[TD([[makeQuery(id+"F2.imprint","IMPRINT",EDGE,{"derivedFrom":subQ0}),1.0]])]});}
            var Q63;
            {var subQ0=sQuery(id+"F2.wireOp",EDGE,"E13.2.46.0");Q63=makeQuery(id+"F2.imprint","IMPRINT",FACE,{"disambiguationData":[TD([[makeQuery(id+"F2.imprint","IMPRINT",EDGE,{"derivedFrom":subQ0}),1.0]])]});}
            var Q64;
            {var subQ0=sQuery(id+"F2.wireOp",EDGE,"E13.2.47.0");Q64=makeQuery(id+"F2.imprint","IMPRINT",FACE,{"disambiguationData":[TD([[makeQuery(id+"F2.imprint","IMPRINT",EDGE,{"derivedFrom":subQ0}),1.0]])]});}
            var Q65;
            {var subQ0=sQuery(id+"F2.wireOp",EDGE,"E13.2.48.0");Q65=makeQuery(id+"F2.imprint","IMPRINT",FACE,{"disambiguationData":[TD([[makeQuery(id+"F2.imprint","IMPRINT",EDGE,{"derivedFrom":subQ0}),1.0]])]});}
            var Q66;
            {var subQ0=sQuery(id+"F2.wireOp",EDGE,"E13.2.49.0");Q66=makeQuery(id+"F2.imprint","IMPRINT",FACE,{"disambiguationData":[TD([[makeQuery(id+"F2.imprint","IMPRINT",EDGE,{"derivedFrom":subQ0}),1.0]])]});}
            var Q67;
            {var subQ0=sQuery(id+"F2.wireOp",EDGE,"E13.2.50.0");Q67=makeQuery(id+"F2.imprint","IMPRINT",FACE,{"disambiguationData":[TD([[makeQuery(id+"F2.imprint","IMPRINT",EDGE,{"derivedFrom":subQ0}),1.0]])]});}
            var Q68;
            {var subQ0=sQuery(id+"F2.wireOp",EDGE,"E13.2.51.0");Q68=makeQuery(id+"F2.imprint","IMPRINT",FACE,{"disambiguationData":[TD([[makeQuery(id+"F2.imprint","IMPRINT",EDGE,{"derivedFrom":subQ0}),1.0]])]});}
            var Q69;
            {var subQ0=sQuery(id+"F2.wireOp",EDGE,"E13.2.52.0");Q69=makeQuery(id+"F2.imprint","IMPRINT",FACE,{"disambiguationData":[TD([[makeQuery(id+"F2.imprint","IMPRINT",EDGE,{"derivedFrom":subQ0}),1.0]])]});}
            var Q70;
            {var subQ0=sQuery(id+"F2.wireOp",EDGE,"E13.2.53.0");Q70=makeQuery(id+"F2.imprint","IMPRINT",FACE,{"disambiguationData":[TD([[makeQuery(id+"F2.imprint","IMPRINT",EDGE,{"derivedFrom":subQ0}),1.0]])]});}
            var Q71;
            {var subQ0=sQuery(id+"F2.wireOp",EDGE,"E13.2.54.0");Q71=makeQuery(id+"F2.imprint","IMPRINT",FACE,{"disambiguationData":[TD([[makeQuery(id+"F2.imprint","IMPRINT",EDGE,{"derivedFrom":subQ0}),1.0]])]});}
            var Q72;
            {var subQ0=sQuery(id+"F2.wireOp",EDGE,"E13.2.55.0");Q72=makeQuery(id+"F2.imprint","IMPRINT",FACE,{"disambiguationData":[TD([[makeQuery(id+"F2.imprint","IMPRINT",EDGE,{"derivedFrom":subQ0}),1.0]])]});}
            var Q73;
            {var subQ0=sQuery(id+"F2.wireOp",EDGE,"E13.2.56.0");Q73=makeQuery(id+"F2.imprint","IMPRINT",FACE,{"disambiguationData":[TD([[makeQuery(id+"F2.imprint","IMPRINT",EDGE,{"derivedFrom":subQ0}),1.0]])]});}
            var Q74;
            {var subQ0=sQuery(id+"F2.wireOp",EDGE,"E13.2.57.0");Q74=makeQuery(id+"F2.imprint","IMPRINT",FACE,{"disambiguationData":[TD([[makeQuery(id+"F2.imprint","IMPRINT",EDGE,{"derivedFrom":subQ0}),1.0]])]});}
            var Q75;
            {var subQ0=sQuery(id+"F2.wireOp",EDGE,"E13.2.58.0");Q75=makeQuery(id+"F2.imprint","IMPRINT",FACE,{"disambiguationData":[TD([[makeQuery(id+"F2.imprint","IMPRINT",EDGE,{"derivedFrom":subQ0}),1.0]])]});}
            var Q76;
            {var subQ0=sQuery(id+"F2.wireOp",EDGE,"E13.2.59.0");Q76=makeQuery(id+"F2.imprint","IMPRINT",FACE,{"disambiguationData":[TD([[makeQuery(id+"F2.imprint","IMPRINT",EDGE,{"derivedFrom":subQ0}),1.0]])]});}
            var Q77;
            {var subQ0=sQuery(id+"F2.wireOp",EDGE,"E13.2.60.0");Q77=makeQuery(id+"F2.imprint","IMPRINT",FACE,{"disambiguationData":[TD([[makeQuery(id+"F2.imprint","IMPRINT",EDGE,{"derivedFrom":subQ0}),1.0]])]});}
            var Q78;
            {var subQ0=sQuery(id+"F2.wireOp",EDGE,"E13.2.63.0");Q78=makeQuery(id+"F2.imprint","IMPRINT",FACE,{"disambiguationData":[TD([[makeQuery(id+"F2.imprint","IMPRINT",EDGE,{"derivedFrom":subQ0}),1.0]])]});}
            var Q79;
            {var subQ0=sQuery(id+"F2.wireOp",EDGE,"E13.2.64.0");Q79=makeQuery(id+"F2.imprint","IMPRINT",FACE,{"disambiguationData":[TD([[makeQuery(id+"F2.imprint","IMPRINT",EDGE,{"derivedFrom":subQ0}),1.0]])]});}
            var Q80;
            {var subQ0=sQuery(id+"F2.wireOp",EDGE,"E13.2.65.0");Q80=makeQuery(id+"F2.imprint","IMPRINT",FACE,{"disambiguationData":[TD([[makeQuery(id+"F2.imprint","IMPRINT",EDGE,{"derivedFrom":subQ0}),1.0]])]});}
            var Q81;
            {var subQ0=sQuery(id+"F2.wireOp",EDGE,"E13.2.66.0");Q81=makeQuery(id+"F2.imprint","IMPRINT",FACE,{"disambiguationData":[TD([[makeQuery(id+"F2.imprint","IMPRINT",EDGE,{"derivedFrom":subQ0}),1.0]])]});}
            var Q82;
            {var subQ0=sQuery(id+"F2.wireOp",EDGE,"E13.2.67.0");Q82=makeQuery(id+"F2.imprint","IMPRINT",FACE,{"disambiguationData":[TD([[makeQuery(id+"F2.imprint","IMPRINT",EDGE,{"derivedFrom":subQ0}),1.0]])]});}
            var Q83;
            {var subQ0=sQuery(id+"F2.wireOp",EDGE,"E13.2.61.0");Q83=makeQuery(id+"F2.imprint","IMPRINT",FACE,{"disambiguationData":[TD([[makeQuery(id+"F2.imprint","IMPRINT",EDGE,{"derivedFrom":subQ0}),1.0]])]});}
            var Q84;
            {var subQ0=sQuery(id+"F2.wireOp",EDGE,"E13.2.62.0");Q84=makeQuery(id+"F2.imprint","IMPRINT",FACE,{"disambiguationData":[TD([[makeQuery(id+"F2.imprint","IMPRINT",EDGE,{"derivedFrom":subQ0}),1.0]])]});}
            var Q85;
            Q85=makeQuery(id+"F1.opRevolve","SWEPT_FACE",FACE,{"disambiguationData":[OSD([sQuery(id+"F0.wireOp",EDGE,"E4")])]});
            extrude(context, id + "F3", {"entities" : qUnion([Q0, Q1, Q2, Q3, Q4, Q5, Q6, Q7, Q8, Q9, Q10, Q11, Q12, Q13, Q14, Q15, Q16, Q17, Q18, Q19, Q20, Q21, Q22, Q23, Q24, Q25, Q26, Q27, Q28, Q29, Q30, Q31, Q32, Q33, Q34, Q35, Q36, Q37, Q38, Q39, Q40, Q41, Q42, Q43, Q44, Q45, Q46, Q47, Q48, Q49, Q50, Q51, Q52, Q53, Q54, Q55, Q56, Q57, Q58, Q59, Q60, Q61, Q62, Q63, Q64, Q65, Q66, Q67, Q68, Q69, Q70, Q71, Q72, Q73, Q74, Q75, Q76, Q77, Q78, Q79, Q80, Q81, Q82, Q83, Q84]), "operationType" : NewBodyOperationType.ADD, "endBound" : BoundingType.UP_TO_SURFACE, "endBoundEntityFace" : qUnion([Q85]), "depth" : 25 * mm});
        }
        {
            var Q0;
            Q0=makeQuery(id+"F1.opRevolve","SWEPT_FACE",FACE,{"disambiguationData":[OSD([sQuery(id+"F0.wireOp",EDGE,"E2")])]});
            var sketch = newSketch(context, id + "F4", { "sketchPlane" : qUnion([Q0])});
            skCircle(sketch, "E16", {"center": v(0, 18) * mm, "radius": 8.5 * mm});
            skCircle(sketch, "E17", {"center": v(0, 18) * mm, "radius": 11 * mm});
            skCircle(sketch, "E18.1.0", {"center": v(-15.59, -9) * mm, "radius": 8.5 * mm});
            skCircle(sketch, "E18.1.1", {"center": v(-15.59, -9) * mm, "radius": 11 * mm});
            skCircle(sketch, "E18.2.0", {"center": v(15.59, -9) * mm, "radius": 8.5 * mm});
            skCircle(sketch, "E18.2.1", {"center": v(15.59, -9) * mm, "radius": 11 * mm});
            skPoint(sketch, "E18.center", {"position": v(0, 0) * mm});
            skSolve(sketch);
        }
        {
            var Q0;
            Q0 = qSketchRegion(id + "F4", true);
            extrude(context, id + "F5", {"entities" : qUnion([Q0]), "operationType" : NewBodyOperationType.ADD, "depth" : 2 * mm});
        }
        {
            var Q0;
            Q0=makeQuery(id+"F5.boolean.opBoolean","SPLIT",FACE,{"disambiguationData":[TD([makeQuery(id+"F1.opRevolve","SWEPT_FACE",FACE,{"disambiguationData":[OSD([sQuery(id+"F0.wireOp",EDGE,"E6.filletArc")])]})])],"derivedFrom":makeQuery(id+"F1.opRevolve","SWEPT_FACE",FACE,{"disambiguationData":[OSD([sQuery(id+"F0.wireOp",EDGE,"E2")])]})});
            var sketch = newSketch(context, id + "F6", { "sketchPlane" : qUnion([Q0])});
            skCircle(sketch, "E19.0.0", {"center": v(0, 18) * mm, "radius": 8.5 * mm});
            skCircle(sketch, "E20.0.0", {"center": v(-15.59, -9) * mm, "radius": 8.5 * mm});
            skCircle(sketch, "E21.0.0", {"center": v(15.59, -9) * mm, "radius": 8.5 * mm});
            skSolve(sketch);
        }
        {
            var Q0;
            Q0 = qSketchRegion(id + "F6", true);
            extrude(context, id + "F7", {"entities" : qUnion([Q0]), "operationType" : NewBodyOperationType.REMOVE, "endBound" : BoundingType.UP_TO_NEXT, "oppositeDirection" : true, "depth" : 25 * mm});
        }
    });
